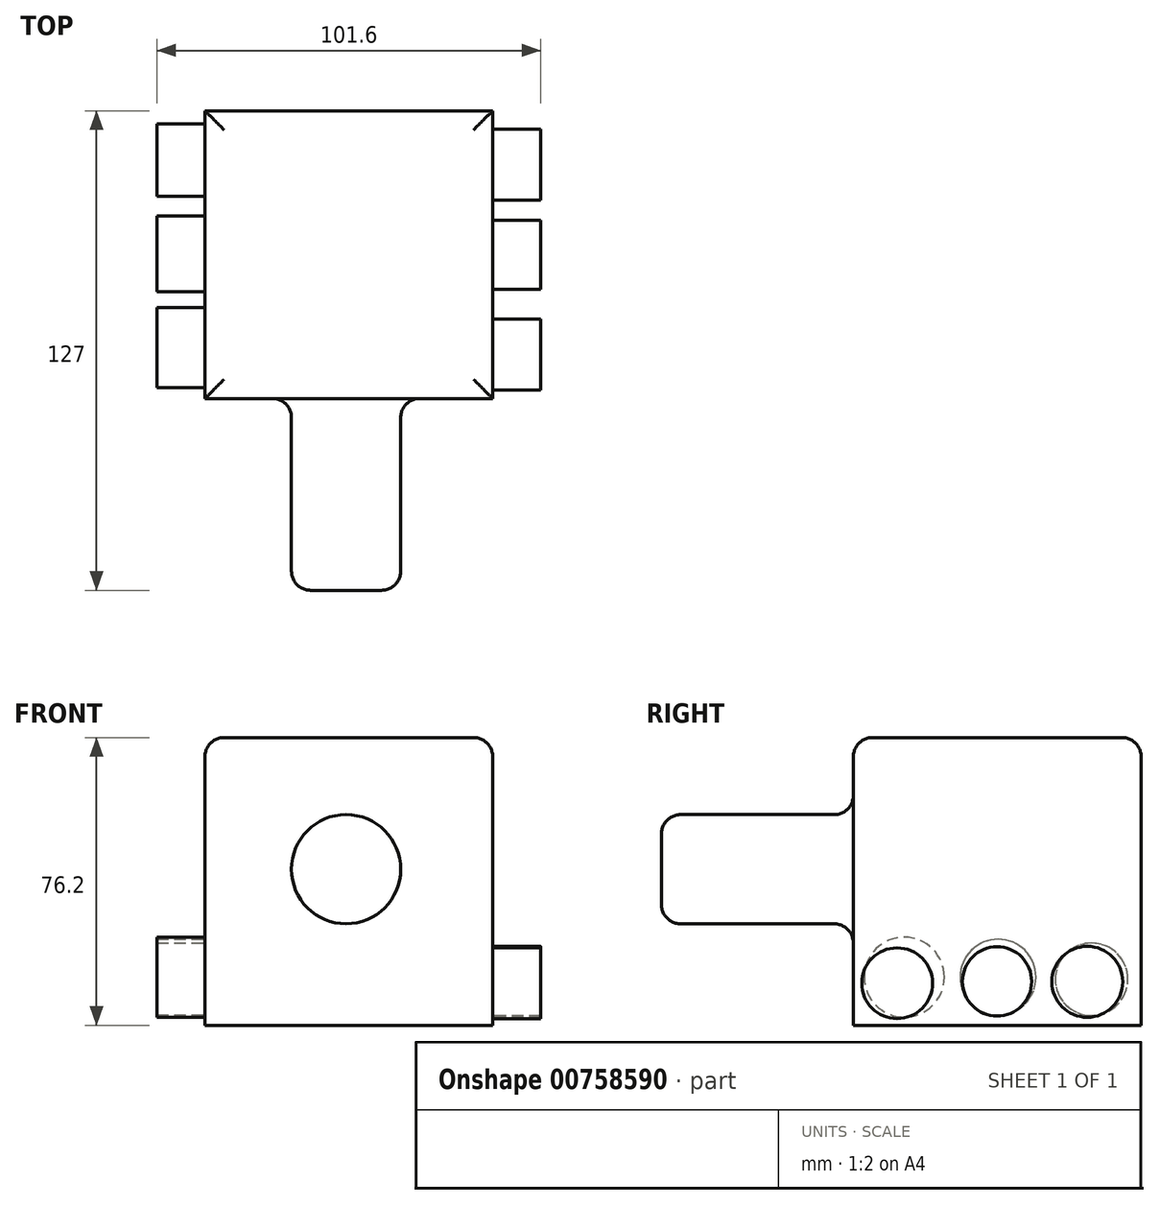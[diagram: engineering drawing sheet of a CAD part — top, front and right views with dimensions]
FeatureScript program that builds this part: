
annotation { "Feature Type Name" : "Feature", "Feature Type Description" : "" }
export const myFeature = defineFeature(function(context is Context, id is Id, definition is map)
    precondition{}
    {
        {
            var Q0;
            Q0=qCreatedBy(makeId("Front.planeOp"),FACE);
            var sketch = newSketch(context, id + "F0", { "sketchPlane" : qUnion([Q0])});
            skLineSegment(sketch, "E0.bottom", {"start": v(-28.24, 44.95) * mm, "end": v(47.96, 44.95) * mm});
            skLineSegment(sketch, "E0.top", {"start": v(-28.24, -31.25) * mm, "end": v(47.96, -31.25) * mm});
            skLineSegment(sketch, "E0.left", {"start": v(-28.24, 44.95) * mm, "end": v(-28.24, -31.25) * mm});
            skLineSegment(sketch, "E0.right", {"start": v(47.96, 44.95) * mm, "end": v(47.96, -31.25) * mm});
            skSolve(sketch);
        }
        {
            var Q0;
            Q0=makeQuery(id+"F0.imprint","IMPRINT",FACE,{"disambiguationData":[TD([[makeQuery(id+"F0.imprint","IMPRINT",EDGE,{"derivedFrom":sQuery(id+"F0.wireOp",EDGE,"E0.bottom")}),-1.0]])]});
            extrude(context, id + "F1", {"entities" : qUnion([Q0]), "depth" : 76.2 * mm, "offsetDistance" : 25.4 * mm});
        }
        {
            var Q0;
            Q0=makeQuery(id+"F1.opExtrude","SWEPT_FACE",FACE,{"disambiguationData":[OSD([sQuery(id+"F0.wireOp",EDGE,"E0.right")])]});
            var sketch = newSketch(context, id + "F2", { "sketchPlane" : qUnion([Q0])});
            skCircle(sketch, "E1", {"center": v(-14.26, -19.74) * mm, "radius": 9.39 * mm});
            skCircle(sketch, "E2", {"center": v(-38.15, -19.65) * mm, "radius": 9.17 * mm});
            skCircle(sketch, "E3", {"center": v(-64.6, -20.12) * mm, "radius": 9.37 * mm});
            skSolve(sketch);
        }
        {
            var Q0;
            Q0=makeQuery(id+"F2.imprint","IMPRINT",FACE,{"disambiguationData":[TD([[makeQuery(id+"F2.imprint","IMPRINT",EDGE,{"derivedFrom":sQuery(id+"F2.wireOp",EDGE,"E3")}),1.0]])]});
            var Q1;
            Q1=makeQuery(id+"F2.imprint","IMPRINT",FACE,{"disambiguationData":[TD([[makeQuery(id+"F2.imprint","IMPRINT",EDGE,{"derivedFrom":sQuery(id+"F2.wireOp",EDGE,"E2")}),1.0]])]});
            var Q2;
            Q2=makeQuery(id+"F2.imprint","IMPRINT",FACE,{"disambiguationData":[TD([[makeQuery(id+"F2.imprint","IMPRINT",EDGE,{"derivedFrom":sQuery(id+"F2.wireOp",EDGE,"E1")}),1.0]])]});
            extrude(context, id + "F3", {"entities" : qUnion([Q0, Q1, Q2]), "operationType" : NewBodyOperationType.ADD, "depth" : 12.7 * mm, "offsetDistance" : 25.4 * mm});
        }
        {
            var Q0;
            Q0=makeQuery(id+"F1.opExtrude","SWEPT_FACE",FACE,{"disambiguationData":[OSD([sQuery(id+"F0.wireOp",EDGE,"E0.left")])]});
            var sketch = newSketch(context, id + "F4", { "sketchPlane" : qUnion([Q0])});
            skCircle(sketch, "E4", {"center": v(62.7, -18.5) * mm, "radius": 10.59 * mm});
            skCircle(sketch, "E5", {"center": v(37.86, -18.5) * mm, "radius": 10.04 * mm});
            skCircle(sketch, "E6", {"center": v(13.12, -19.08) * mm, "radius": 9.6 * mm});
            skSolve(sketch);
        }
        {
            var Q0;
            Q0=makeQuery(id+"F4.imprint","IMPRINT",FACE,{"disambiguationData":[TD([[makeQuery(id+"F4.imprint","IMPRINT",EDGE,{"derivedFrom":sQuery(id+"F4.wireOp",EDGE,"E6")}),1.0]])]});
            var Q1;
            Q1=makeQuery(id+"F4.imprint","IMPRINT",FACE,{"disambiguationData":[TD([[makeQuery(id+"F4.imprint","IMPRINT",EDGE,{"derivedFrom":sQuery(id+"F4.wireOp",EDGE,"E5")}),1.0]])]});
            var Q2;
            Q2=makeQuery(id+"F4.imprint","IMPRINT",FACE,{"disambiguationData":[TD([[makeQuery(id+"F4.imprint","IMPRINT",EDGE,{"derivedFrom":sQuery(id+"F4.wireOp",EDGE,"E4")}),1.0]])]});
            extrude(context, id + "F5", {"entities" : qUnion([Q0, Q1, Q2]), "operationType" : NewBodyOperationType.ADD, "depth" : 12.7 * mm, "offsetDistance" : 25.4 * mm});
        }
        {
            var Q0;
            Q0=makeQuery(id+"F1.opExtrude","CAP_FACE",FACE,{"disambiguationData":[OSD([sQuery(id+"F0.wireOp",EDGE,"E0.bottom"),sQuery(id+"F0.wireOp",EDGE,"E0.top"),sQuery(id+"F0.wireOp",EDGE,"E0.left"),sQuery(id+"F0.wireOp",EDGE,"E0.right")])],"isStart":false});
            var sketch = newSketch(context, id + "F6", { "sketchPlane" : qUnion([Q0])});
            skPoint(sketch, "E7", {"position": v(9.43, 10.3) * mm});
            skSolve(sketch);
        }
        {
            var Q0;
            Q0=makeQuery(id+"F6.imprint","IMPRINT",FACE,{"disambiguationData":[TD([[makeQuery(id+"F6.imprint","IMPRINT",EDGE,{"derivedFrom":makeQuery(id+"F1.opExtrude","CAP_EDGE",EDGE,{"disambiguationData":[OSD([sQuery(id+"F0.wireOp",EDGE,"E0.bottom")])],"isStart":false})}),-1.0]])]});
            var sketch = newSketch(context, id + "F7", { "sketchPlane" : qUnion([Q0])});
            skCircle(sketch, "E8", {"center": v(9.14, 10.07) * mm, "radius": 14.46 * mm});
            skSolve(sketch);
        }
        {
            var Q0;
            Q0=makeQuery(id+"F7.imprint","IMPRINT",FACE,{"disambiguationData":[TD([[makeQuery(id+"F7.imprint","IMPRINT",EDGE,{"derivedFrom":sQuery(id+"F7.wireOp",EDGE,"E8")}),1.0]])]});
            extrude(context, id + "F8", {"entities" : qUnion([Q0]), "operationType" : NewBodyOperationType.ADD, "depth" : 50.8 * mm, "offsetDistance" : 25.4 * mm});
        }
        {
            var Q0;
            Q0=makeQuery(id+"F8.opExtrude","SWEPT_FACE",FACE,{"disambiguationData":[OSD([sQuery(id+"F7.wireOp",EDGE,"E8")])]});
            fillet(context, id + "F9", {"entities" : qUnion([Q0]), "radius" : 5.08 * mm, "tangentPropagation" : true, "allowEdgeOverflow" : false});
        }
        {
            var Q0;
            Q0=makeQuery(id+"F1.opExtrude","SWEPT_FACE",FACE,{"disambiguationData":[OSD([sQuery(id+"F0.wireOp",EDGE,"E0.bottom")])]});
            fillet(context, id + "F10", {"entities" : qUnion([Q0]), "radius" : 5.08 * mm, "tangentPropagation" : true, "allowEdgeOverflow" : false});
        }
    });
